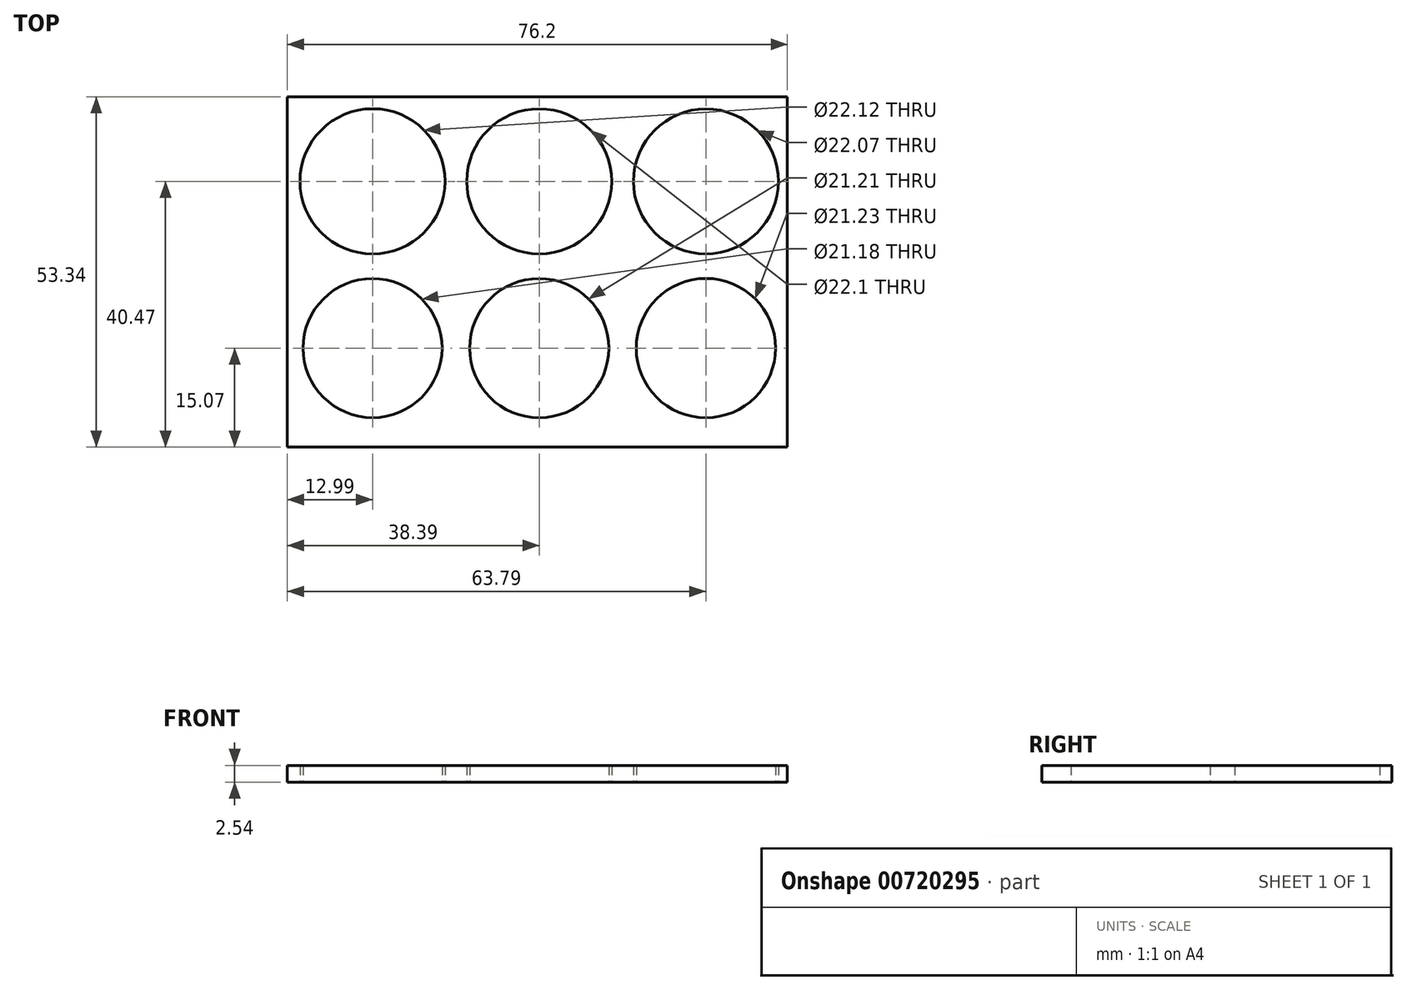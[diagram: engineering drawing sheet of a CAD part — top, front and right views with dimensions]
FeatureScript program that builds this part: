
annotation { "Feature Type Name" : "Feature", "Feature Type Description" : "" }
export const myFeature = defineFeature(function(context is Context, id is Id, definition is map)
    precondition{}
    {
        {
            var Q0;
            Q0=qCreatedBy(makeId("Top.planeOp"),FACE);
            var sketch = newSketch(context, id + "F0", { "sketchPlane" : qUnion([Q0])});
            skPoint(sketch, "E0.middle", {"position": v(0, 0) * mm});
            skCircle(sketch, "E1", {"center": v(0, 0) * mm, "radius": 10.6 * mm});
            skLineSegment(sketch, "E2", {"start": v(0, 0) * mm, "end": v(-25.4, 0) * mm});
            skLineSegment(sketch, "E3", {"start": v(0, 0) * mm, "end": v(25.4, 0) * mm});
            skCircle(sketch, "E4", {"center": v(-25.4, 0) * mm, "radius": 10.6 * mm});
            skCircle(sketch, "E5", {"center": v(25.4, 0) * mm, "radius": 10.62 * mm});
            skLineSegment(sketch, "E6", {"start": v(37.8, 12.87) * mm, "end": v(37.8, -15.07) * mm});
            skLineSegment(sketch, "E7", {"start": v(37.8, -15.07) * mm, "end": v(-38.4, -15.07) * mm});
            skLineSegment(sketch, "E8", {"start": v(-38.4, -15.07) * mm, "end": v(-38.4, 12.87) * mm});
            skLineSegment(sketch, "E9", {"start": v(-38.4, 12.87) * mm, "end": v(37.8, 12.87) * mm});
            skLineSegment(sketch, "E10", {"start": v(0, 0) * mm, "end": v(0, 25.4) * mm});
            skCircle(sketch, "E11", {"center": v(0, 25.4) * mm, "radius": 11.05 * mm});
            skLineSegment(sketch, "E12", {"start": v(0, 25.4) * mm, "end": v(-25.4, 25.4) * mm});
            skLineSegment(sketch, "E13", {"start": v(0, 25.4) * mm, "end": v(25.4, 25.4) * mm});
            skCircle(sketch, "E14", {"center": v(-25.4, 25.4) * mm, "radius": 11.06 * mm});
            skCircle(sketch, "E15", {"center": v(25.4, 25.4) * mm, "radius": 11.04 * mm});
            skLineSegment(sketch, "E16", {"start": v(-38.4, 12.87) * mm, "end": v(-38.4, 38.27) * mm});
            skLineSegment(sketch, "E17", {"start": v(37.8, 12.87) * mm, "end": v(37.8, 38.27) * mm});
            skLineSegment(sketch, "E18", {"start": v(-38.4, 38.27) * mm, "end": v(37.8, 38.27) * mm});
            skSolve(sketch);
        }
        {
            var Q0;
            Q0=makeQuery(id+"F0.imprint","IMPRINT",FACE,{"disambiguationData":[TD([[makeQuery(id+"F0.imprint","IMPRINT",EDGE,{"derivedFrom":sQuery(id+"F0.wireOp",EDGE,"E4")}),-1.0]])]});
            var Q1;
            Q1=makeQuery(id+"F0.imprint","IMPRINT",FACE,{"disambiguationData":[TD([[makeQuery(id+"F0.imprint","IMPRINT",EDGE,{"derivedFrom":sQuery(id+"F0.wireOp",EDGE,"E14")}),-1.0]])]});
            extrude(context, id + "F1", {"entities" : qUnion([Q0, Q1]), "depth" : 2.54 * mm, "offsetDistance" : 25.4 * mm});
        }
    });
